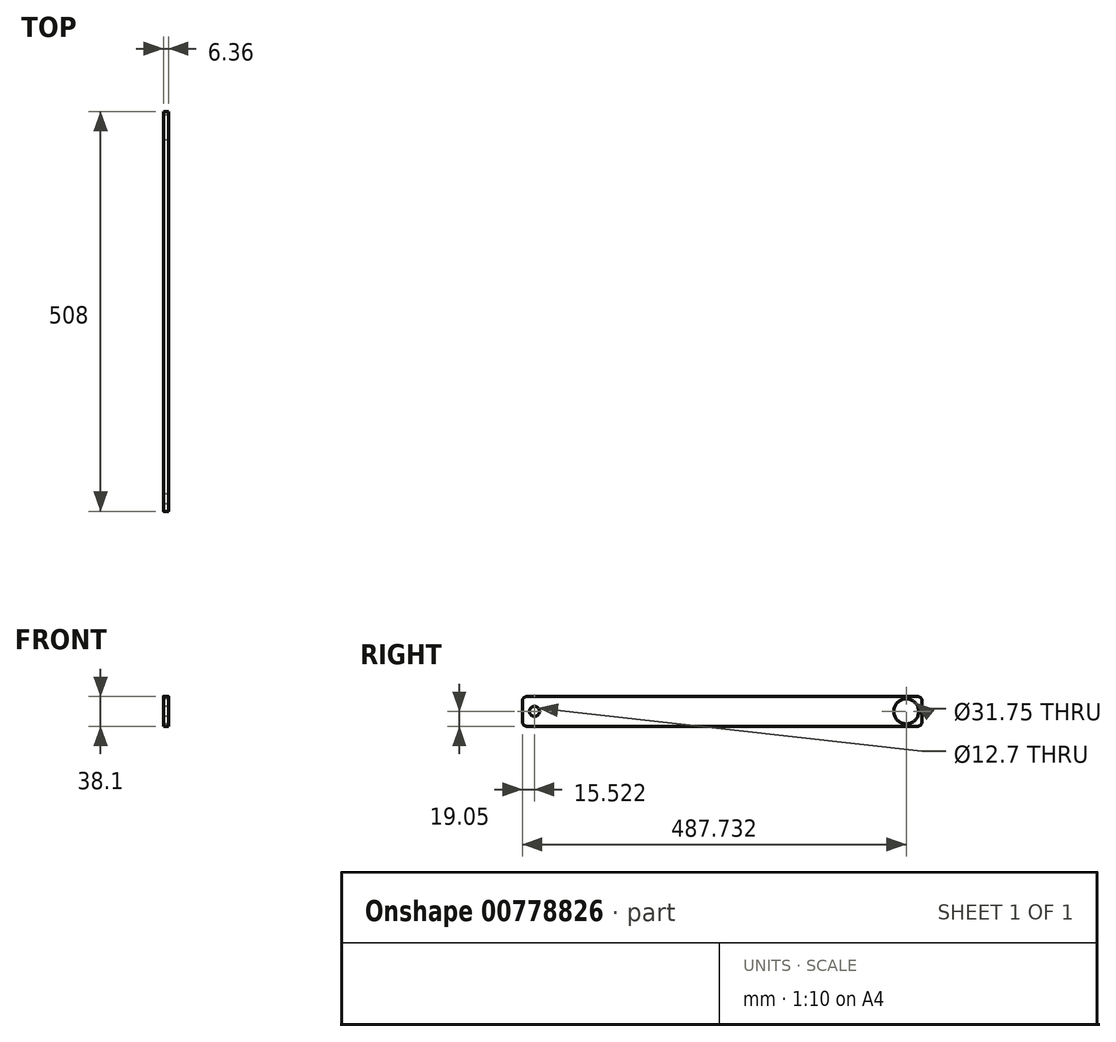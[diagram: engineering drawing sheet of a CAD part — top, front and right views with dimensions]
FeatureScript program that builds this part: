
annotation { "Feature Type Name" : "Feature", "Feature Type Description" : "" }
export const myFeature = defineFeature(function(context is Context, id is Id, definition is map)
    precondition{}
    {
        {
            var Q0;
            Q0=qCreatedBy(makeId("Right.planeOp"),FACE);
            var sketch = newSketch(context, id + "F0", { "sketchPlane" : qUnion([Q0])});
            skLineSegment(sketch, "E0.bottom", {"start": v(-247.65, 19.05) * mm, "end": v(247.65, 19.05) * mm});
            skLineSegment(sketch, "E0.top", {"start": v(-247.65, -19.05) * mm, "end": v(247.65, -19.05) * mm});
            skLineSegment(sketch, "E0.left", {"start": v(-254, 12.7) * mm, "end": v(-254, -12.7) * mm});
            skLineSegment(sketch, "E0.right", {"start": v(254, 12.7) * mm, "end": v(254, -12.7) * mm});
            skPoint(sketch, "E0.middle", {"position": v(0, 0) * mm});
            skCircle(sketch, "E1", {"center": v(233.73, 0) * mm, "radius": 15.88 * mm});
            skPoint(sketch, "E1.centerSnap0", {"position": v(254, 0) * mm});
            skCircle(sketch, "E2", {"center": v(-238.48, 0) * mm, "radius": 6.35 * mm});
            skPoint(sketch, "E3.visualSharp", {"position": v(-254, 19.05) * mm});
            skArc(sketch, "E3.filletArc", {"start": v(-247.65, 19.05) * mm, "mid": v(-252.14, 17.2) * mm, "end": v(-254, 12.7) * mm});
            skPoint(sketch, "E4.visualSharp", {"position": v(-254, -19.05) * mm});
            skArc(sketch, "E4.filletArc", {"start": v(-254, -12.7) * mm, "mid": v(-252.14, -17.2) * mm, "end": v(-247.65, -19.05) * mm});
            skPoint(sketch, "E5.visualSharp", {"position": v(254, -19.05) * mm});
            skArc(sketch, "E5.filletArc", {"start": v(247.65, -19.05) * mm, "mid": v(252.14, -17.2) * mm, "end": v(254, -12.7) * mm});
            skPoint(sketch, "E6.visualSharp", {"position": v(254, 19.05) * mm});
            skArc(sketch, "E6.filletArc", {"start": v(254, 12.7) * mm, "mid": v(252.14, 17.2) * mm, "end": v(247.65, 19.05) * mm});
            skSolve(sketch);
        }
        {
            var Q0;
            Q0 = qSketchRegion(id + "F0", true);
            extrude(context, id + "F1", {"entities" : qUnion([Q0]), "endBound" : BoundingType.SYMMETRIC, "depth" : 6.35 * mm, "offsetDistance" : 25.4 * mm});
        }
    });
